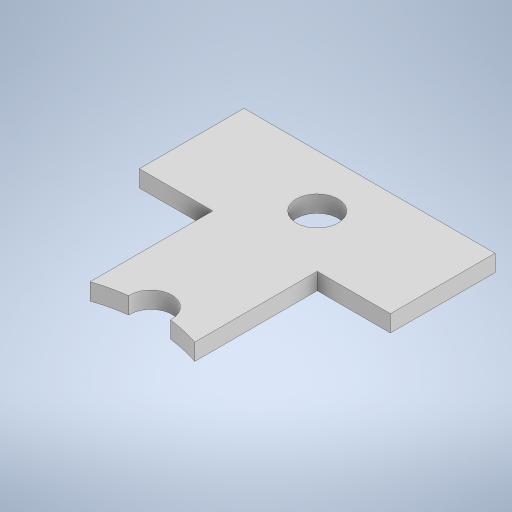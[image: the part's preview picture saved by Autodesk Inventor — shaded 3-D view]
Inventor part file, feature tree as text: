
AUTODESK INVENTOR PART (.ipt)
format: ipt  version: 2024.1 (Build 281209000, 209)  size: 249,856 bytes
history: native  units: mm
features: extrude x2, sketch x2, other x1, projected_geometry x1
ambient origin geometry x8: Origin, YZ Plane, XZ Plane, XY Plane, X Axis, Y Axis, Z Axis, Center Point
bodies: Body1 (feature_tree)
feature tree (6):
  other  "ソリッド1"
  extrude  "押し出し1"  Depth=114.0mm
  extrude  "押し出し2"  Depth=45.0mm
  sketch  "スケッチ1"
  sketch  "スケッチ2"
  projected_geometry  "投影ループ1"
